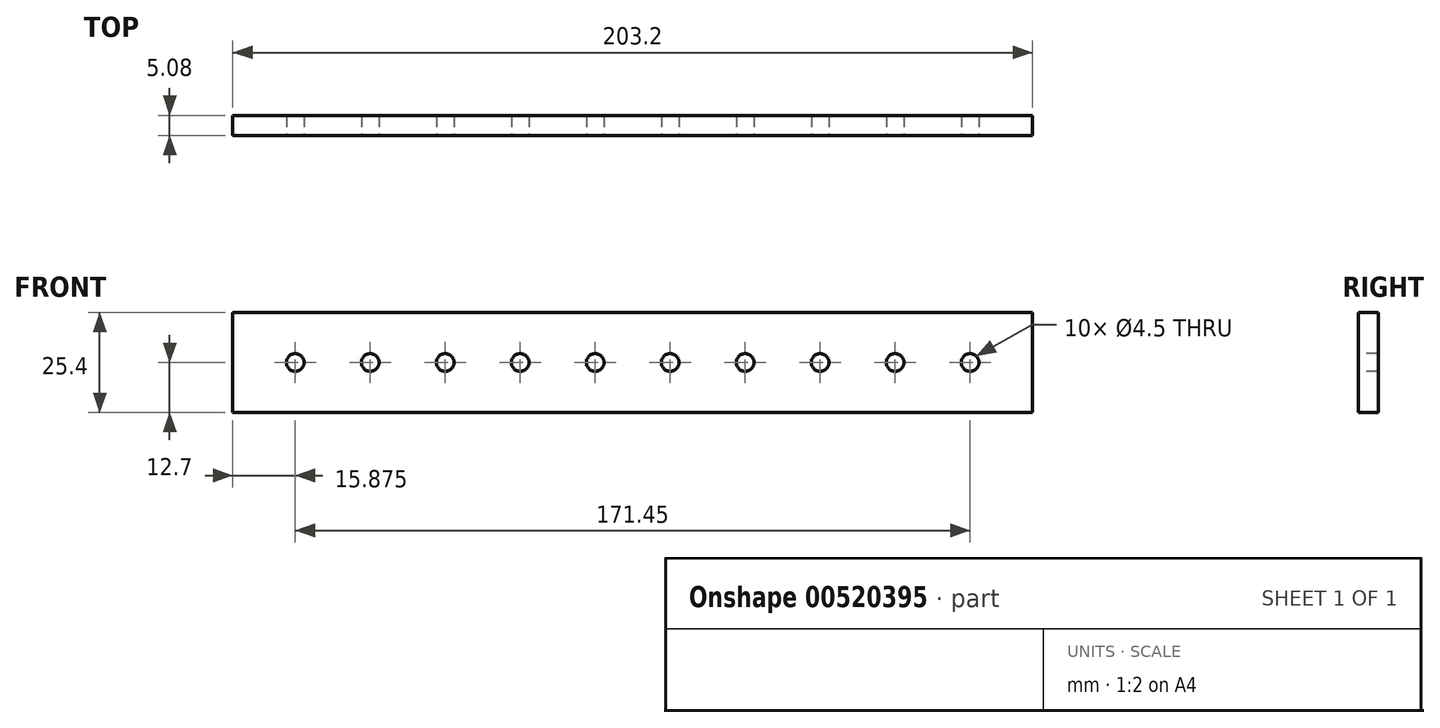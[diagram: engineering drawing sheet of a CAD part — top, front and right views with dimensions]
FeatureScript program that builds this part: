
annotation { "Feature Type Name" : "Feature", "Feature Type Description" : "" }
export const myFeature = defineFeature(function(context is Context, id is Id, definition is map)
    precondition{}
    {
        {
            var Q0;
            Q0=qCreatedBy(makeId("Front.planeOp"),FACE);
            var sketch = newSketch(context, id + "F0", { "sketchPlane" : qUnion([Q0])});
            skLineSegment(sketch, "E0.bottom", {"start": v(-101.6, 12.7) * mm, "end": v(101.6, 12.7) * mm});
            skLineSegment(sketch, "E0.top", {"start": v(-101.6, -12.7) * mm, "end": v(101.6, -12.7) * mm});
            skLineSegment(sketch, "E0.left", {"start": v(-101.6, 12.7) * mm, "end": v(-101.6, -12.7) * mm});
            skLineSegment(sketch, "E0.right", {"start": v(101.6, 12.7) * mm, "end": v(101.6, -12.7) * mm});
            skPoint(sketch, "E0.middle", {"position": v(0, 0) * mm});
            skLineSegment(sketch, "E1", {"start": v(-220.71, 0) * mm, "end": v(262.76, 0) * mm, "construction": true});
            skSolve(sketch);
        }
        {
            var Q0;
            Q0 = qSketchRegion(id + "F0", true);
            extrude(context, id + "F1", {"entities" : qUnion([Q0]), "depth" : 5.08 * mm, "offsetDistance" : 25.4 * mm});
        }
        {
            var Q0;
            Q0=makeQuery(id+"F1.opExtrude","CAP_FACE",FACE,{"disambiguationData":[OSD([sQuery(id+"F0.wireOp",EDGE,"E0.bottom"),sQuery(id+"F0.wireOp",EDGE,"E0.top"),sQuery(id+"F0.wireOp",EDGE,"E0.left"),sQuery(id+"F0.wireOp",EDGE,"E0.right")])],"isStart":false});
            var sketch = newSketch(context, id + "F2", { "sketchPlane" : qUnion([Q0])});
            skLineSegment(sketch, "E2", {"start": v(-155.75, 0) * mm, "end": v(137.43, 0) * mm, "construction": true});
            skCircle(sketch, "E3", {"center": v(-85.73, 0) * mm, "radius": 2.25 * mm});
            skCircle(sketch, "E4.1.0.0", {"center": v(-66.68, 0) * mm, "radius": 2.25 * mm});
            skCircle(sketch, "E4.2.0.0", {"center": v(-47.63, 0) * mm, "radius": 2.25 * mm});
            skCircle(sketch, "E4.3.0.0", {"center": v(-28.58, 0) * mm, "radius": 2.25 * mm});
            skCircle(sketch, "E4.4.0.0", {"center": v(-9.53, 0) * mm, "radius": 2.25 * mm});
            skCircle(sketch, "E4.5.0.0", {"center": v(9.52, 0) * mm, "radius": 2.25 * mm});
            skCircle(sketch, "E4.6.0.0", {"center": v(28.57, 0) * mm, "radius": 2.25 * mm});
            skCircle(sketch, "E4.7.0.0", {"center": v(47.62, 0) * mm, "radius": 2.25 * mm});
            skCircle(sketch, "E4.8.0.0", {"center": v(66.67, 0) * mm, "radius": 2.25 * mm});
            skCircle(sketch, "E4.9.0.0", {"center": v(85.72, 0) * mm, "radius": 2.25 * mm});
            skLineSegment(sketch, "E4.direction1", {"start": v(-85.73, 0) * mm, "end": v(-66.68, 0) * mm, "construction": true});
            skSolve(sketch);
        }
        {
            var Q0;
            Q0 = qSketchRegion(id + "F2", true);
            extrude(context, id + "F3", {"entities" : qUnion([Q0]), "operationType" : NewBodyOperationType.REMOVE, "oppositeDirection" : true, "depth" : 25.4 * mm, "offsetDistance" : 25.4 * mm});
        }
    });
